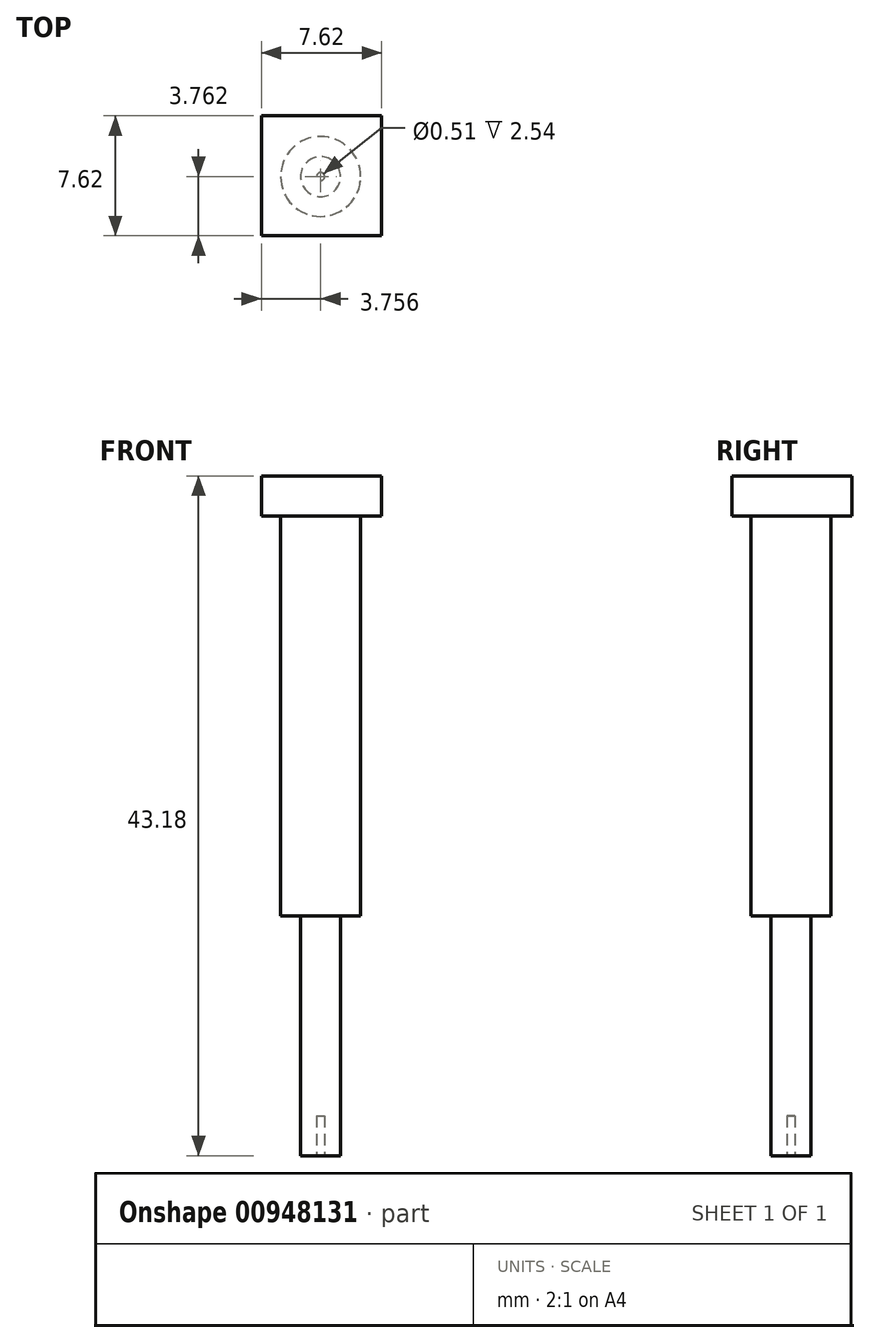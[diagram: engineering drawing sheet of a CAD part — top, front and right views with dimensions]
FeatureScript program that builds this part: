
annotation { "Feature Type Name" : "Feature", "Feature Type Description" : "" }
export const myFeature = defineFeature(function(context is Context, id is Id, definition is map)
    precondition{}
    {
        {
            var Q0;
            Q0=qCreatedBy(makeId("Top.planeOp"),FACE);
            var sketch = newSketch(context, id + "F0", { "sketchPlane" : qUnion([Q0])});
            skLineSegment(sketch, "E0.bottom", {"start": v(-42.6, -18.03) * mm, "end": v(-34.99, -18.03) * mm});
            skLineSegment(sketch, "E0.top", {"start": v(-42.6, -25.65) * mm, "end": v(-34.99, -25.65) * mm});
            skLineSegment(sketch, "E0.left", {"start": v(-42.6, -18.03) * mm, "end": v(-42.6, -25.65) * mm});
            skLineSegment(sketch, "E0.right", {"start": v(-34.99, -18.03) * mm, "end": v(-34.99, -25.65) * mm});
            skSolve(sketch);
        }
        {
            var Q0;
            Q0 = qSketchRegion(id + "F0", true);
            extrude(context, id + "F1", {"entities" : qUnion([Q0]), "depth" : 2.54 * mm, "offsetDistance" : 25.4 * mm});
        }
        {
            var Q0;
            Q0=makeQuery(id+"F1.opExtrude","CAP_FACE",FACE,{"disambiguationData":[OSD([sQuery(id+"F0.wireOp",EDGE,"E0.bottom"),sQuery(id+"F0.wireOp",EDGE,"E0.top"),sQuery(id+"F0.wireOp",EDGE,"E0.left"),sQuery(id+"F0.wireOp",EDGE,"E0.right")])],"isStart":true});
            var sketch = newSketch(context, id + "F2", { "sketchPlane" : qUnion([Q0])});
            skCircle(sketch, "E1", {"center": v(-38.85, 21.89) * mm, "radius": 2.54 * mm});
            skCircle(sketch, "E2", {"center": v(-38.85, 21.89) * mm, "radius": 1.27 * mm});
            skSolve(sketch);
        }
        {
            var Q0;
            Q0=makeQuery(id+"F2.imprint","IMPRINT",FACE,{"disambiguationData":[TD([[makeQuery(id+"F2.imprint","IMPRINT",EDGE,{"derivedFrom":sQuery(id+"F2.wireOp",EDGE,"E2")}),1.0]])]});
            extrude(context, id + "F3", {"entities" : qUnion([Q0]), "operationType" : NewBodyOperationType.ADD, "depth" : 40.64 * mm, "offsetDistance" : 25.4 * mm});
        }
        {
            var Q0;
            Q0=makeQuery(id+"F3.opExtrude","CAP_FACE",FACE,{"disambiguationData":[OSD([sQuery(id+"F2.wireOp",EDGE,"E2")])],"isStart":false});
            var sketch = newSketch(context, id + "F4", { "sketchPlane" : qUnion([Q0])});
            skCircle(sketch, "E3", {"center": v(-38.85, 21.89) * mm, "radius": 0.25 * mm});
            skSolve(sketch);
        }
        {
            var Q0;
            Q0 = qSketchRegion(id + "F4", true);
            extrude(context, id + "F5", {"entities" : qUnion([Q0]), "operationType" : NewBodyOperationType.REMOVE, "oppositeDirection" : true, "depth" : 2.54 * mm, "offsetDistance" : 25.4 * mm});
        }
        {
            var Q0;
            Q0 = qSketchRegion(id + "F2", true);
            extrude(context, id + "F6", {"entities" : qUnion([Q0]), "operationType" : NewBodyOperationType.ADD, "depth" : 25.4 * mm, "offsetDistance" : 25.4 * mm});
        }
    });
